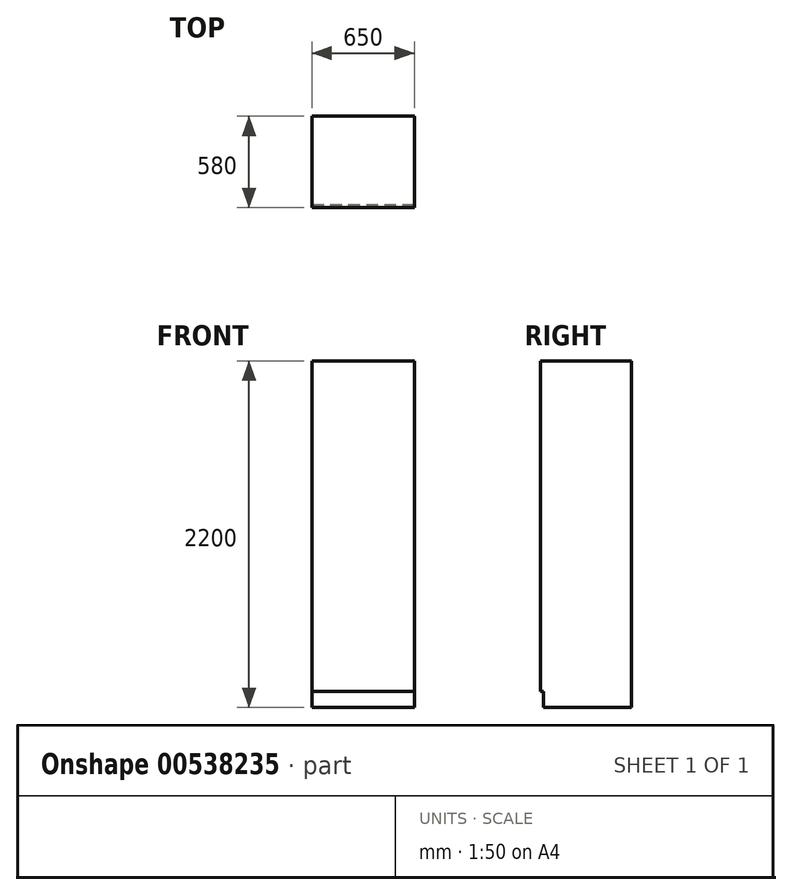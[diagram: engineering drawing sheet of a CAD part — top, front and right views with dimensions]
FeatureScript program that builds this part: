
annotation { "Feature Type Name" : "Feature", "Feature Type Description" : "" }
export const myFeature = defineFeature(function(context is Context, id is Id, definition is map)
    precondition{}
    {
        {
            var Q0;
            Q0=qCreatedBy(makeId("Top.planeOp"),FACE);
            var sketch = newSketch(context, id + "F0", { "sketchPlane" : qUnion([Q0])});
            skLineSegment(sketch, "E0.bottom", {"start": v(0, 0) * mm, "end": v(-650, 0) * mm});
            skLineSegment(sketch, "E0.top", {"start": v(0, 580) * mm, "end": v(-650, 580) * mm});
            skLineSegment(sketch, "E0.left", {"start": v(0, 0) * mm, "end": v(0, 580) * mm});
            skLineSegment(sketch, "E0.right", {"start": v(-650, 0) * mm, "end": v(-650, 580) * mm});
            skSolve(sketch);
        }
        {
            var Q0;
            Q0 = qSketchRegion(id + "F0", true);
            extrude(context, id + "F1", {"entities" : qUnion([Q0]), "depth" : 2200 * mm, "offsetDistance" : 25 * mm});
        }
        {
            var Q0;
            Q0=makeQuery(id+"F1.opExtrude","SWEPT_FACE",FACE,{"disambiguationData":[OSD([sQuery(id+"F0.wireOp",EDGE,"E0.right")])]});
            var sketch = newSketch(context, id + "F2", { "sketchPlane" : qUnion([Q0])});
            skLineSegment(sketch, "E1.bottom", {"start": v(115.4, -83.96) * mm, "end": v(-20, -83.96) * mm});
            skLineSegment(sketch, "E1.top", {"start": v(115.4, 100) * mm, "end": v(-20, 100) * mm});
            skLineSegment(sketch, "E1.left", {"start": v(115.4, -83.96) * mm, "end": v(115.4, 100) * mm});
            skLineSegment(sketch, "E1.right", {"start": v(-20, -83.96) * mm, "end": v(-20, 100) * mm});
            skSolve(sketch);
        }
        {
            var Q0;
            Q0 = qSketchRegion(id + "F2", true);
            extrude(context, id + "F3", {"entities" : qUnion([Q0]), "operationType" : NewBodyOperationType.REMOVE, "endBound" : BoundingType.THROUGH_ALL, "oppositeDirection" : true, "depth" : 25 * mm, "offsetDistance" : 25 * mm});
        }
    });
